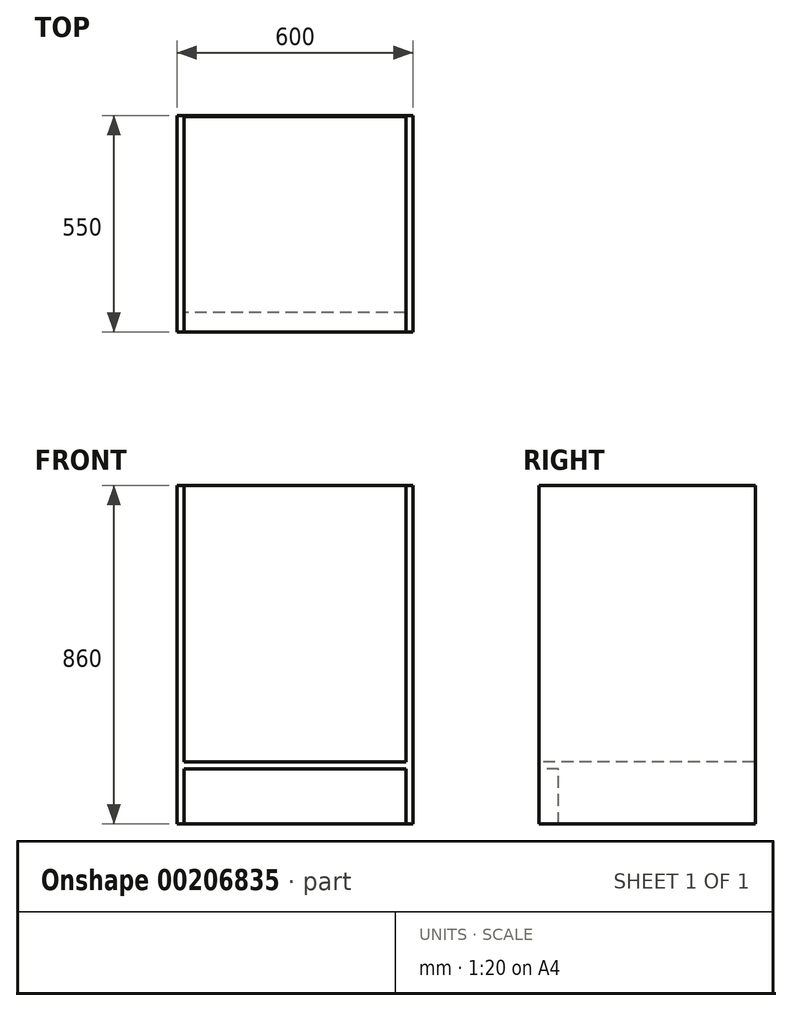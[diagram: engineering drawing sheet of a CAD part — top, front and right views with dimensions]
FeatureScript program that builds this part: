
annotation { "Feature Type Name" : "Feature", "Feature Type Description" : "" }
export const myFeature = defineFeature(function(context is Context, id is Id, definition is map)
    precondition{}
    {
        {
            var Q0;
            Q0=qCreatedBy(makeId("Top.planeOp"),FACE);
            var sketch = newSketch(context, id + "F0", { "sketchPlane" : qUnion([Q0])});
            skLineSegment(sketch, "E0.bottom", {"start": v(-518.83, 504.1) * mm, "end": v(81.17, 504.1) * mm});
            skLineSegment(sketch, "E0.top", {"start": v(-518.83, -45.9) * mm, "end": v(-500.83, -45.9) * mm});
            skLineSegment(sketch, "E0.left", {"start": v(-518.83, 504.1) * mm, "end": v(-518.83, -45.9) * mm});
            skLineSegment(sketch, "E0.right", {"start": v(81.17, 504.1) * mm, "end": v(81.17, -45.9) * mm});
            skLineSegment(sketch, "E1.bottom", {"start": v(-500.83, 501.1) * mm, "end": v(63.17, 501.1) * mm});
            skLineSegment(sketch, "E1.left", {"start": v(-500.83, 501.1) * mm, "end": v(-500.83, -45.9) * mm});
            skLineSegment(sketch, "E1.right", {"start": v(63.17, 501.1) * mm, "end": v(63.17, -45.9) * mm});
            skLineSegment(sketch, "E2.trimOffspring", {"start": v(63.17, -45.9) * mm, "end": v(81.17, -45.9) * mm});
            skSolve(sketch);
        }
        {
            var Q0;
            Q0=qCreatedBy(makeId("Top.planeOp"),FACE);
            var sketch = newSketch(context, id + "F1", { "sketchPlane" : qUnion([Q0])});
            skPoint(sketch, "E3.0", {"position": v(-518.83, 504.1) * mm});
            skLineSegment(sketch, "E4.0", {"start": v(-518.83, 504.1) * mm, "end": v(-518.83, -45.9) * mm});
            skLineSegment(sketch, "E5.0", {"start": v(-518.83, 504.1) * mm, "end": v(81.17, 504.1) * mm});
            skLineSegment(sketch, "E6.0", {"start": v(81.17, 504.1) * mm, "end": v(81.17, -45.9) * mm});
            skLineSegment(sketch, "E7", {"start": v(-518.83, -45.9) * mm, "end": v(81.17, -45.9) * mm});
            skSolve(sketch);
        }
        {
            var Q0;
            Q0 = qSketchRegion(id + "F0", true);
            extrude(context, id + "F2", {"entities" : qUnion([Q0]), "depth" : 720 * mm});
        }
        {
            var Q0;
            Q0 = qSketchRegion(id + "F1", true);
            extrude(context, id + "F3", {"entities" : qUnion([Q0]), "operationType" : NewBodyOperationType.ADD, "depth" : 18 * mm});
        }
        {
            var Q0;
            Q0=qCreatedBy(makeId("Top.planeOp"),FACE);
            var sketch = newSketch(context, id + "F4", { "sketchPlane" : qUnion([Q0])});
            skLineSegment(sketch, "E8.0", {"start": v(-518.83, 504.1) * mm, "end": v(-518.83, -45.9) * mm});
            skLineSegment(sketch, "E9.0", {"start": v(-518.83, 504.1) * mm, "end": v(81.17, 504.1) * mm});
            skLineSegment(sketch, "E10.0", {"start": v(81.17, 504.1) * mm, "end": v(81.17, -45.9) * mm});
            skLineSegment(sketch, "E11.0", {"start": v(-518.83, -45.9) * mm, "end": v(-500.83, -45.9) * mm});
            skLineSegment(sketch, "E12.0", {"start": v(63.17, -45.9) * mm, "end": v(81.17, -45.9) * mm});
            skLineSegment(sketch, "E13", {"start": v(63.17, -45.9) * mm, "end": v(63.17, 4.1) * mm});
            skLineSegment(sketch, "E14", {"start": v(63.17, 4.1) * mm, "end": v(-500.83, 4.1) * mm});
            skLineSegment(sketch, "E15", {"start": v(-500.83, 4.1) * mm, "end": v(-500.83, -45.9) * mm});
            skSolve(sketch);
        }
        {
            var Q0;
            Q0 = qSketchRegion(id + "F4", true);
            extrude(context, id + "F5", {"entities" : qUnion([Q0]), "operationType" : NewBodyOperationType.ADD, "oppositeDirection" : true, "depth" : 140 * mm});
        }
    });
